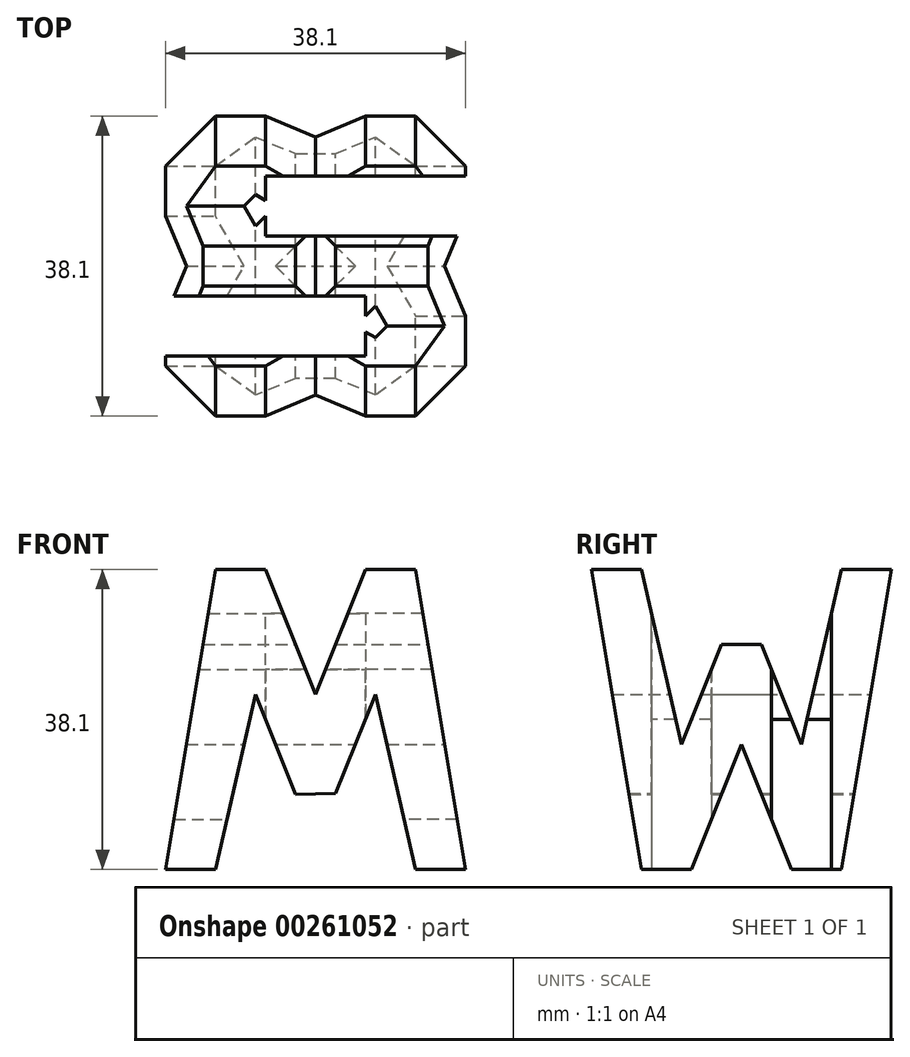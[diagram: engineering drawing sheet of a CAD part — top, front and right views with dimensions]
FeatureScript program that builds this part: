
annotation { "Feature Type Name" : "Feature", "Feature Type Description" : "" }
export const myFeature = defineFeature(function(context is Context, id is Id, definition is map)
    precondition{}
    {
        {
            var Q0;
            Q0=qCreatedBy(makeId("Front.planeOp"),FACE);
            var sketch = newSketch(context, id + "F0", { "sketchPlane" : qUnion([Q0])});
            skLineSegment(sketch, "E0", {"start": v(0, 0) * mm, "end": v(0, 38.1) * mm});
            skLineSegment(sketch, "E1", {"start": v(0, 38.1) * mm, "end": v(38.1, 38.1) * mm});
            skLineSegment(sketch, "E2", {"start": v(38.1, 38.1) * mm, "end": v(38.1, 0) * mm});
            skLineSegment(sketch, "E3", {"start": v(38.1, 0) * mm, "end": v(0, 0) * mm});
            skSolve(sketch);
        }
        {
            var Q0;
            Q0 = qSketchRegion(id + "F0", true);
            extrude(context, id + "F1", {"entities" : qUnion([Q0]), "depth" : 38.1 * mm});
        }
        {
            var Q0;
            Q0=qCreatedBy(makeId("Top.planeOp"),FACE);
            cPlane(context, id + "F2", {"entities" : qUnion([Q0]), "cplaneType" : CPlaneType.OFFSET, "offset" : 38.1 * mm, "width" : 152.4 * mm, "height" : 152.4 * mm});
        }
        {
            var Q0;
            Q0=qCreatedBy(makeId("Right.planeOp"),FACE);
            cPlane(context, id + "F3", {"entities" : qUnion([Q0]), "cplaneType" : CPlaneType.OFFSET, "offset" : 38.1 * mm, "width" : 152.4 * mm, "height" : 152.4 * mm});
        }
        {
            var Q0;
            Q0=qCreatedBy(makeId("Front.planeOp"),FACE);
            cPlane(context, id + "F4", {"entities" : qUnion([Q0]), "cplaneType" : CPlaneType.OFFSET, "offset" : 38.1 * mm, "width" : 152.4 * mm, "height" : 152.4 * mm});
        }
        {
            var Q0;
            Q0=qCreatedBy(id+"F3.planeOp",FACE);
            var sketch = newSketch(context, id + "F5", { "sketchPlane" : qUnion([Q0])});
            skLineSegment(sketch, "E4", {"start": v(0, 0) * mm, "end": v(0, 38.1) * mm});
            skLineSegment(sketch, "E5", {"start": v(0, 38.1) * mm, "end": v(-38.1, 38.1) * mm});
            skLineSegment(sketch, "E6", {"start": v(-38.1, 38.1) * mm, "end": v(-38.1, 0) * mm});
            skLineSegment(sketch, "E7", {"start": v(-38.1, 0) * mm, "end": v(0, 0) * mm});
            skLineSegment(sketch, "E8", {"start": v(-38.1, 38.1) * mm, "end": v(-31.75, 0) * mm});
            skLineSegment(sketch, "E9", {"start": v(-6.35, 0) * mm, "end": v(0, 38.1) * mm});
            skLineSegment(sketch, "E10", {"start": v(-31.75, 38.1) * mm, "end": v(-26.67, 15.88) * mm});
            skLineSegment(sketch, "E11", {"start": v(-26.67, 15.87) * mm, "end": v(-21.59, 28.57) * mm});
            skLineSegment(sketch, "E12", {"start": v(-21.59, 28.58) * mm, "end": v(-16.5, 28.58) * mm});
            skLineSegment(sketch, "E13", {"start": v(-16.5, 28.58) * mm, "end": v(-11.43, 15.88) * mm});
            skLineSegment(sketch, "E14", {"start": v(-11.43, 15.88) * mm, "end": v(-6.35, 38.1) * mm});
            skLineSegment(sketch, "E15", {"start": v(-31.75, 0) * mm, "end": v(-25.4, 0) * mm});
            skLineSegment(sketch, "E16", {"start": v(-25.4, 0) * mm, "end": v(-19.05, 15.87) * mm});
            skLineSegment(sketch, "E17", {"start": v(-19.05, 15.87) * mm, "end": v(-12.7, 0) * mm});
            skLineSegment(sketch, "E18", {"start": v(-12.7, 0) * mm, "end": v(-6.35, 0) * mm});
            skSolve(sketch);
        }
        {
            var Q0;
            {var subQ0=sQuery(id+"F5.wireOp",EDGE,"E10");Q0=makeQuery(id+"F5.imprint","IMPRINT",FACE,{"disambiguationData":[TD([[makeQuery(id+"F5.imprint","IMPRINT",EDGE,{"derivedFrom":subQ0}),1.0]])]});}
            var Q1;
            {var subQ0=sQuery(id+"F5.wireOp",EDGE,"E6");Q1=makeQuery(id+"F5.imprint","IMPRINT",FACE,{"disambiguationData":[TD([[makeQuery(id+"F5.imprint","IMPRINT",EDGE,{"derivedFrom":subQ0}),1.0]])]});}
            var Q2;
            {var subQ0=sQuery(id+"F5.wireOp",EDGE,"E16");Q2=makeQuery(id+"F5.imprint","IMPRINT",FACE,{"disambiguationData":[TD([[makeQuery(id+"F5.imprint","IMPRINT",EDGE,{"derivedFrom":subQ0}),-1.0]])]});}
            var Q3;
            {var subQ0=sQuery(id+"F5.wireOp",EDGE,"E4");Q3=makeQuery(id+"F5.imprint","IMPRINT",FACE,{"disambiguationData":[TD([[makeQuery(id+"F5.imprint","IMPRINT",EDGE,{"derivedFrom":subQ0}),1.0]])]});}
            extrude(context, id + "F6", {"entities" : qUnion([Q0, Q1, Q2, Q3]), "operationType" : NewBodyOperationType.REMOVE, "oppositeDirection" : true, "depth" : 38.1 * mm});
        }
        {
            var Q0;
            Q0=qCreatedBy(makeId("Front.planeOp"),FACE);
            var sketch = newSketch(context, id + "F7", { "sketchPlane" : qUnion([Q0])});
            skLineSegment(sketch, "E19", {"start": v(0, 0) * mm, "end": v(38.1, 0) * mm});
            skLineSegment(sketch, "E20", {"start": v(38.1, 0) * mm, "end": v(38.1, 38.1) * mm});
            skLineSegment(sketch, "E21", {"start": v(38.1, 38.1) * mm, "end": v(0, 38.1) * mm});
            skLineSegment(sketch, "E22", {"start": v(0, 38.1) * mm, "end": v(0, 0) * mm});
            skLineSegment(sketch, "E23", {"start": v(0, 0) * mm, "end": v(6.35, 38.1) * mm});
            skLineSegment(sketch, "E24", {"start": v(12.7, 38.1) * mm, "end": v(19.05, 22.22) * mm});
            skLineSegment(sketch, "E25", {"start": v(19.05, 22.23) * mm, "end": v(25.4, 38.1) * mm});
            skLineSegment(sketch, "E26", {"start": v(38.1, 0) * mm, "end": v(31.75, 38.1) * mm});
            skLineSegment(sketch, "E27", {"start": v(6.35, 0) * mm, "end": v(11.43, 22.23) * mm});
            skLineSegment(sketch, "E28", {"start": v(11.43, 22.23) * mm, "end": v(16.51, 9.52) * mm});
            skLineSegment(sketch, "E29", {"start": v(21.6, 9.65) * mm, "end": v(26.67, 22.23) * mm});
            skLineSegment(sketch, "E30", {"start": v(16.51, 9.52) * mm, "end": v(21.6, 9.65) * mm});
            skLineSegment(sketch, "E31", {"start": v(26.67, 22.23) * mm, "end": v(31.75, 0) * mm});
            skSolve(sketch);
        }
        {
            var Q0;
            {var subQ0=sQuery(id+"F7.wireOp",EDGE,"E27");Q0=makeQuery(id+"F7.imprint","IMPRINT",FACE,{"disambiguationData":[TD([[makeQuery(id+"F7.imprint","IMPRINT",EDGE,{"derivedFrom":subQ0}),-1.0]])]});}
            var Q1;
            {var subQ0=sQuery(id+"F7.wireOp",EDGE,"E20");Q1=makeQuery(id+"F7.imprint","IMPRINT",FACE,{"disambiguationData":[TD([[makeQuery(id+"F7.imprint","IMPRINT",EDGE,{"derivedFrom":subQ0}),1.0]])]});}
            var Q2;
            {var subQ0=sQuery(id+"F7.wireOp",EDGE,"E24");Q2=makeQuery(id+"F7.imprint","IMPRINT",FACE,{"disambiguationData":[TD([[makeQuery(id+"F7.imprint","IMPRINT",EDGE,{"derivedFrom":subQ0}),1.0]])]});}
            var Q3;
            {var subQ0=sQuery(id+"F7.wireOp",EDGE,"E22");Q3=makeQuery(id+"F7.imprint","IMPRINT",FACE,{"disambiguationData":[TD([[makeQuery(id+"F7.imprint","IMPRINT",EDGE,{"derivedFrom":subQ0}),1.0]])]});}
            extrude(context, id + "F8", {"entities" : qUnion([Q0, Q1, Q2, Q3]), "operationType" : NewBodyOperationType.REMOVE, "depth" : 38.1 * mm});
        }
        {
            var Q0;
            Q0=qCreatedBy(id+"F2.planeOp",FACE);
            var sketch = newSketch(context, id + "F9", { "sketchPlane" : qUnion([Q0])});
            skLineSegment(sketch, "E32", {"start": v(0, 0) * mm, "end": v(0, -38.1) * mm});
            skLineSegment(sketch, "E33", {"start": v(0, -38.1) * mm, "end": v(38.1, -38.1) * mm});
            skLineSegment(sketch, "E34", {"start": v(38.1, -38.1) * mm, "end": v(38.1, 0) * mm});
            skLineSegment(sketch, "E35", {"start": v(38.1, 0) * mm, "end": v(0, 0) * mm});
            skLineSegment(sketch, "E36", {"start": v(12.7, -7.62) * mm, "end": v(12.7, -15.24) * mm});
            skLineSegment(sketch, "E37", {"start": v(12.7, -15.24) * mm, "end": v(38.1, -15.24) * mm});
            skLineSegment(sketch, "E38", {"start": v(12.7, -7.62) * mm, "end": v(38.1, -7.62) * mm});
            skLineSegment(sketch, "E39", {"start": v(25.4, -22.86) * mm, "end": v(25.4, -30.48) * mm});
            skLineSegment(sketch, "E40", {"start": v(25.4, -30.48) * mm, "end": v(0, -30.48) * mm});
            skLineSegment(sketch, "E41", {"start": v(25.4, -22.86) * mm, "end": v(0, -22.86) * mm});
            skPoint(sketch, "E41.endSnap0", {"position": v(0, -19.05) * mm});
            skSolve(sketch);
        }
        {
            var Q0;
            Q0=makeQuery(id+"F9.imprint","IMPRINT",FACE,{"disambiguationData":[TD([[makeQuery(id+"F9.imprint","IMPRINT",EDGE,{"derivedFrom":sQuery(id+"F9.wireOp",EDGE,"E36")}),1.0]])]});
            var Q1;
            Q1=makeQuery(id+"F9.imprint","IMPRINT",FACE,{"disambiguationData":[TD([[makeQuery(id+"F9.imprint","IMPRINT",EDGE,{"derivedFrom":sQuery(id+"F9.wireOp",EDGE,"E39")}),-1.0]])]});
            extrude(context, id + "F10", {"entities" : qUnion([Q0, Q1]), "operationType" : NewBodyOperationType.REMOVE, "oppositeDirection" : true, "depth" : 38.1 * mm});
        }
    });
